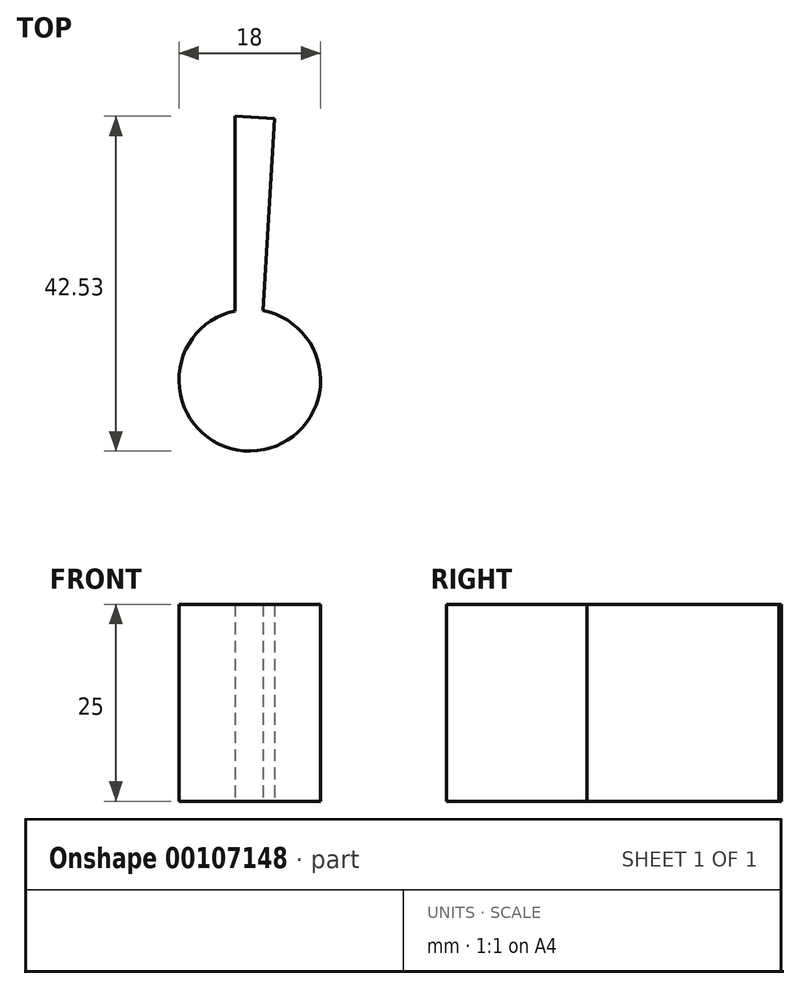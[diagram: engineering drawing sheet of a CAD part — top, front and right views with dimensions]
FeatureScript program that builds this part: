
annotation { "Feature Type Name" : "Feature", "Feature Type Description" : "" }
export const myFeature = defineFeature(function(context is Context, id is Id, definition is map)
    precondition{}
    {
        {
            var Q0;
            Q0=qCreatedBy(makeId("Top.planeOp"),FACE);
            var sketch = newSketch(context, id + "F0", { "sketchPlane" : qUnion([Q0])});
            skCircle(sketch, "E0", {"center": v(0, 0) * mm, "radius": 9 * mm});
            skLineSegment(sketch, "E1", {"start": v(-1.87, 8.8) * mm, "end": v(-1.87, 33.53) * mm});
            skLineSegment(sketch, "E2", {"start": v(-1.87, 33.53) * mm, "end": v(3.14, 33.22) * mm});
            skLineSegment(sketch, "E3", {"start": v(3.14, 33.22) * mm, "end": v(1.67, 8.84) * mm});
            skSolve(sketch);
        }
        {
            var Q0;
            Q0 = qSketchRegion(id + "F0", true);
            var Q1;
            {var subQ0=sQuery(id+"F0.wireOp",EDGE,"E0");var subQ1=makeQuery(id+"F0.imprint","INTERSECT",VERTEX,{"derivedFrom":[subQ0,sQuery(id+"F0.wireOp",EDGE,"E1")]});Q1=makeQuery(id+"F0.imprint","IMPRINT",FACE,{"disambiguationData":[TD([[makeQuery(id+"F0.imprint","IMPRINT",EDGE,{"disambiguationData":[TD([[subQ1,1.0]])],"derivedFrom":subQ0}),1.0]])]});}
            extrude(context, id + "F1", {"entities" : qUnion([Q0, Q1]), "depth" : 25 * mm});
        }
    });
